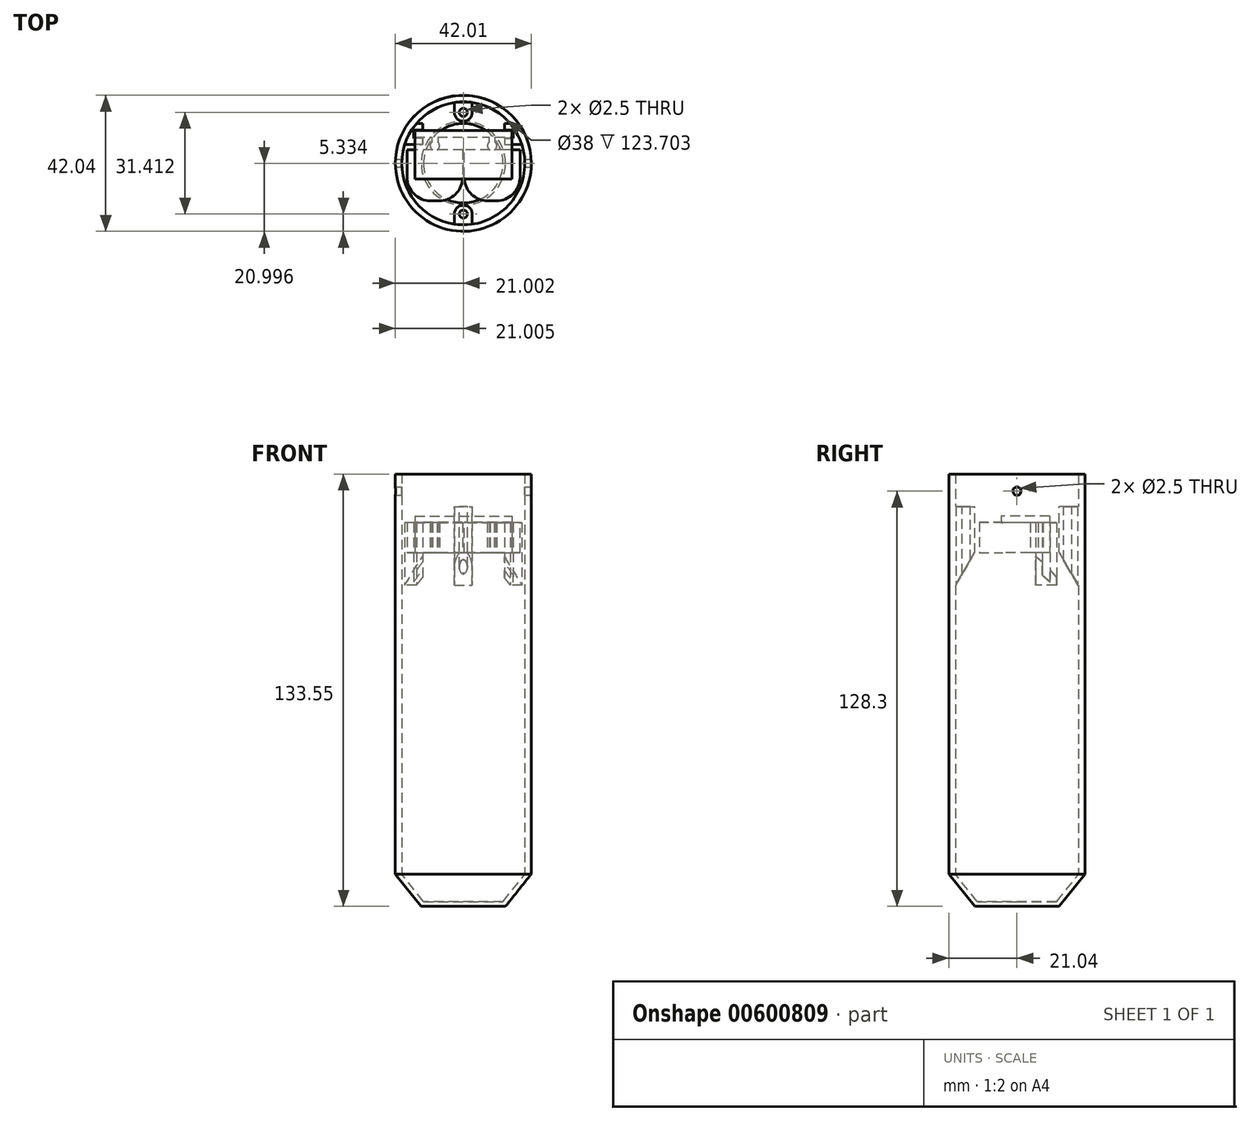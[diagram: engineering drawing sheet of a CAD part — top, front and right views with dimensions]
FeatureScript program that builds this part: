
annotation { "Feature Type Name" : "Feature", "Feature Type Description" : "" }
export const myFeature = defineFeature(function(context is Context, id is Id, definition is map)
    precondition{}
    {
        {
            var Q0;
            Q0=qCreatedBy(makeId("Front.planeOp"),FACE);
            var sketch = newSketch(context, id + "F0", { "sketchPlane" : qUnion([Q0])});
            skLineSegment(sketch, "E0.bottom", {"start": v(-22.87, 37.15) * mm, "end": v(-5.67, 37.15) * mm});
            skLineSegment(sketch, "E0.top", {"start": v(-22.87, -71.55) * mm, "end": v(-5.67, -71.55) * mm});
            skLineSegment(sketch, "E0.left", {"start": v(-22.87, 37.15) * mm, "end": v(-22.87, -71.55) * mm});
            skLineSegment(sketch, "E0.right", {"start": v(-5.67, 37.15) * mm, "end": v(-5.67, -71.55) * mm});
            skLineSegment(sketch, "E1.bottom", {"start": v(-5.17, -71.55) * mm, "end": v(12.03, -71.55) * mm});
            skLineSegment(sketch, "E1.top", {"start": v(-5.17, 37.15) * mm, "end": v(12.03, 37.15) * mm});
            skLineSegment(sketch, "E1.left", {"start": v(-5.17, -71.55) * mm, "end": v(-5.17, 37.15) * mm});
            skLineSegment(sketch, "E1.right", {"start": v(12.03, -71.55) * mm, "end": v(12.03, 37.15) * mm});
            skSolve(sketch);
        }
        {
            var Q0;
            Q0=makeQuery(id+"F0.imprint","IMPRINT",FACE,{"disambiguationData":[TD([[makeQuery(id+"F0.imprint","IMPRINT",EDGE,{"derivedFrom":sQuery(id+"F0.wireOp",EDGE,"E0.bottom")}),-1.0]])]});
            var Q1;
            Q1=makeQuery(id+"F0.imprint","IMPRINT",FACE,{"disambiguationData":[TD([[makeQuery(id+"F0.imprint","IMPRINT",EDGE,{"derivedFrom":sQuery(id+"F0.wireOp",EDGE,"E1.bottom")}),1.0]])]});
            extrude(context, id + "F1", {"entities" : qUnion([Q0, Q1]), "depth" : 15.75 * mm, "offsetDistance" : 25 * mm});
        }
        {
            var Q0;
            Q0=makeQuery(id+"F1.opExtrude","CAP_EDGE",EDGE,{"disambiguationData":[OSD([sQuery(id+"F0.wireOp",EDGE,"E0.left")])],"isStart":false});
            var Q1;
            Q1=makeQuery(id+"F1.opExtrude","CAP_EDGE",EDGE,{"disambiguationData":[OSD([sQuery(id+"F0.wireOp",EDGE,"E0.right")])],"isStart":false});
            var Q2;
            Q2=makeQuery(id+"F1.opExtrude","CAP_EDGE",EDGE,{"disambiguationData":[OSD([sQuery(id+"F0.wireOp",EDGE,"E1.left")])],"isStart":false});
            var Q3;
            Q3=makeQuery(id+"F1.opExtrude","CAP_EDGE",EDGE,{"disambiguationData":[OSD([sQuery(id+"F0.wireOp",EDGE,"E1.right")])],"isStart":false});
            fillet(context, id + "F2", {"entities" : qUnion([Q0, Q1, Q2, Q3]), "radius" : 7.3 * mm, "tangentPropagation" : true, "allowEdgeOverflow" : false});
        }
        {
            var Q0;
            Q0=makeQuery(id+"F1.opExtrude","CAP_FACE",FACE,{"disambiguationData":[OSD([sQuery(id+"F0.wireOp",EDGE,"E0.bottom"),sQuery(id+"F0.wireOp",EDGE,"E0.top"),sQuery(id+"F0.wireOp",EDGE,"E0.left"),sQuery(id+"F0.wireOp",EDGE,"E0.right")])],"isStart":true});
            var sketch = newSketch(context, id + "F3", { "sketchPlane" : qUnion([Q0])});
            skLineSegment(sketch, "E2.bottom", {"start": v(11.37, 24.15) * mm, "end": v(17.17, 24.15) * mm});
            skLineSegment(sketch, "E2.top", {"start": v(11.37, 20.15) * mm, "end": v(17.17, 20.15) * mm});
            skLineSegment(sketch, "E2.left", {"start": v(11.37, 24.15) * mm, "end": v(11.37, 20.15) * mm});
            skLineSegment(sketch, "E2.right", {"start": v(17.17, 24.15) * mm, "end": v(17.17, 20.15) * mm});
            skLineSegment(sketch, "E3.bottom", {"start": v(11.37, -15.1) * mm, "end": v(17.17, -15.1) * mm});
            skLineSegment(sketch, "E3.top", {"start": v(11.37, -19.1) * mm, "end": v(17.17, -19.1) * mm});
            skLineSegment(sketch, "E3.left", {"start": v(11.37, -15.1) * mm, "end": v(11.37, -19.1) * mm});
            skLineSegment(sketch, "E3.right", {"start": v(17.17, -15.1) * mm, "end": v(17.17, -19.1) * mm});
            skLineSegment(sketch, "E4.bottom", {"start": v(11.37, -54.35) * mm, "end": v(17.17, -54.35) * mm});
            skLineSegment(sketch, "E4.top", {"start": v(11.37, -58.35) * mm, "end": v(17.17, -58.35) * mm});
            skLineSegment(sketch, "E4.left", {"start": v(11.37, -54.35) * mm, "end": v(11.37, -58.35) * mm});
            skLineSegment(sketch, "E4.right", {"start": v(17.17, -54.35) * mm, "end": v(17.17, -58.35) * mm});
            skLineSegment(sketch, "E5.bottom", {"start": v(-6.33, 24.15) * mm, "end": v(-0.53, 24.15) * mm});
            skLineSegment(sketch, "E5.top", {"start": v(-6.33, 20.15) * mm, "end": v(-0.53, 20.15) * mm});
            skLineSegment(sketch, "E5.left", {"start": v(-6.33, 24.15) * mm, "end": v(-6.33, 20.15) * mm});
            skLineSegment(sketch, "E5.right", {"start": v(-0.53, 24.15) * mm, "end": v(-0.53, 20.15) * mm});
            skPoint(sketch, "E6.oppositeSnap0", {"position": v(-0.53, 22.15) * mm});
            skLineSegment(sketch, "E6.bottom", {"start": v(-6.33, -15.1) * mm, "end": v(-0.53, -15.1) * mm});
            skLineSegment(sketch, "E6.top", {"start": v(-6.33, -19.1) * mm, "end": v(-0.53, -19.1) * mm});
            skLineSegment(sketch, "E6.left", {"start": v(-6.33, -15.1) * mm, "end": v(-6.33, -19.1) * mm});
            skLineSegment(sketch, "E6.right", {"start": v(-0.53, -15.1) * mm, "end": v(-0.53, -19.1) * mm});
            skLineSegment(sketch, "E7.bottom", {"start": v(-6.33, -54.35) * mm, "end": v(-0.53, -54.35) * mm});
            skLineSegment(sketch, "E7.top", {"start": v(-6.33, -58.35) * mm, "end": v(-0.53, -58.35) * mm});
            skLineSegment(sketch, "E7.left", {"start": v(-6.33, -54.35) * mm, "end": v(-6.33, -58.35) * mm});
            skLineSegment(sketch, "E7.right", {"start": v(-0.53, -54.35) * mm, "end": v(-0.53, -58.35) * mm});
            skSolve(sketch);
        }
        {
            var Q0;
            Q0=makeQuery(id+"F3.imprint","IMPRINT",FACE,{"disambiguationData":[TD([[makeQuery(id+"F3.imprint","IMPRINT",EDGE,{"derivedFrom":sQuery(id+"F3.wireOp",EDGE,"E5.bottom")}),-1.0]])]});
            var Q1;
            Q1=makeQuery(id+"F3.imprint","IMPRINT",FACE,{"disambiguationData":[TD([[makeQuery(id+"F3.imprint","IMPRINT",EDGE,{"derivedFrom":sQuery(id+"F3.wireOp",EDGE,"E2.bottom")}),-1.0]])]});
            var Q2;
            Q2=makeQuery(id+"F3.imprint","IMPRINT",FACE,{"disambiguationData":[TD([[makeQuery(id+"F3.imprint","IMPRINT",EDGE,{"derivedFrom":sQuery(id+"F3.wireOp",EDGE,"E6.bottom")}),-1.0]])]});
            var Q3;
            Q3=makeQuery(id+"F3.imprint","IMPRINT",FACE,{"disambiguationData":[TD([[makeQuery(id+"F3.imprint","IMPRINT",EDGE,{"derivedFrom":sQuery(id+"F3.wireOp",EDGE,"E3.bottom")}),-1.0]])]});
            var Q4;
            Q4=makeQuery(id+"F3.imprint","IMPRINT",FACE,{"disambiguationData":[TD([[makeQuery(id+"F3.imprint","IMPRINT",EDGE,{"derivedFrom":sQuery(id+"F3.wireOp",EDGE,"E7.bottom")}),-1.0]])]});
            var Q5;
            Q5=makeQuery(id+"F3.imprint","IMPRINT",FACE,{"disambiguationData":[TD([[makeQuery(id+"F3.imprint","IMPRINT",EDGE,{"derivedFrom":sQuery(id+"F3.wireOp",EDGE,"E4.bottom")}),-1.0]])]});
            extrude(context, id + "F4", {"entities" : qUnion([Q0, Q1, Q2, Q3, Q4, Q5]), "depth" : 3 * mm, "offsetDistance" : 25 * mm});
        }
        {
            var Q0;
            Q0=makeQuery(id+"F4.opExtrude","SWEPT_FACE",FACE,{"disambiguationData":[OSD([sQuery(id+"F3.wireOp",EDGE,"E2.bottom")])]});
            var sketch = newSketch(context, id + "F5", { "sketchPlane" : qUnion([Q0])});
            skCircle(sketch, "E8", {"center": v(-14.27, 1.3) * mm, "radius": 2 * mm});
            skPoint(sketch, "E8.centerSnap0", {"position": v(-14.27, 0) * mm});
            skCircle(sketch, "E9", {"center": v(3.43, 1.3) * mm, "radius": 2 * mm});
            skLineSegment(sketch, "E10", {"start": v(3.43, -0.32) * mm, "end": v(3.43, 2.34) * mm, "construction": true});
            skLineSegment(sketch, "E11", {"start": v(-14.27, 1.3) * mm, "end": v(3.43, 1.3) * mm, "construction": true});
            skSolve(sketch);
        }
        {
            var Q0;
            {var subQ0=sQuery(id+"F5.wireOp",EDGE,"E8");var subQ1=sQuery(id+"F3.wireOp",EDGE,"E2.bottom");var subQ2=makeQuery(id+"F4.opExtrude","CAP_EDGE",EDGE,{"disambiguationData":[OSD([subQ1])],"isStart":false});var subQ3=makeQuery(id+"F5.imprint","INTERSECT",VERTEX,{"disambiguationData":[OD(0.0)],"derivedFrom":[subQ2,subQ0]});Q0=makeQuery(id+"F5.imprint","IMPRINT",FACE,{"disambiguationData":[TD([[makeQuery(id+"F5.imprint","IMPRINT",EDGE,{"disambiguationData":[TD([[subQ3,-1.0]])],"derivedFrom":subQ0}),1.0]])]});}
            extrude(context, id + "F6", {"entities" : qUnion([Q0]), "operationType" : NewBodyOperationType.REMOVE, "oppositeDirection" : true, "depth" : 111.1 * mm, "offsetDistance" : 25 * mm});
        }
        {
            var Q0;
            Q0=makeQuery(id+"F5.imprint","IMPRINT",FACE,{"disambiguationData":[TD([[makeQuery(id+"F5.imprint","IMPRINT",EDGE,{"derivedFrom":sQuery(id+"F5.wireOp",EDGE,"E9")}),1.0]])]});
            extrude(context, id + "F7", {"entities" : qUnion([Q0]), "operationType" : NewBodyOperationType.REMOVE, "oppositeDirection" : true, "depth" : 101.7 * mm, "offsetDistance" : 25 * mm});
        }
        {
            var Q0;
            Q0=makeQuery(id+"F4.opExtrude","CAP_EDGE",EDGE,{"disambiguationData":[OSD([sQuery(id+"F3.wireOp",EDGE,"E2.left")])],"isStart":false});
            var Q1;
            Q1=makeQuery(id+"F4.opExtrude","CAP_EDGE",EDGE,{"disambiguationData":[OSD([sQuery(id+"F3.wireOp",EDGE,"E2.right")])],"isStart":false});
            var Q2;
            Q2=makeQuery(id+"F4.opExtrude","CAP_EDGE",EDGE,{"disambiguationData":[OSD([sQuery(id+"F3.wireOp",EDGE,"E3.left")])],"isStart":false});
            var Q3;
            Q3=makeQuery(id+"F4.opExtrude","CAP_EDGE",EDGE,{"disambiguationData":[OSD([sQuery(id+"F3.wireOp",EDGE,"E3.right")])],"isStart":false});
            var Q4;
            Q4=makeQuery(id+"F4.opExtrude","CAP_EDGE",EDGE,{"disambiguationData":[OSD([sQuery(id+"F3.wireOp",EDGE,"E4.left")])],"isStart":false});
            var Q5;
            Q5=makeQuery(id+"F4.opExtrude","CAP_EDGE",EDGE,{"disambiguationData":[OSD([sQuery(id+"F3.wireOp",EDGE,"E4.right")])],"isStart":false});
            var Q6;
            Q6=makeQuery(id+"F4.opExtrude","CAP_EDGE",EDGE,{"disambiguationData":[OSD([sQuery(id+"F3.wireOp",EDGE,"E7.left")])],"isStart":false});
            var Q7;
            Q7=makeQuery(id+"F4.opExtrude","CAP_EDGE",EDGE,{"disambiguationData":[OSD([sQuery(id+"F3.wireOp",EDGE,"E7.right")])],"isStart":false});
            var Q8;
            Q8=makeQuery(id+"F4.opExtrude","CAP_EDGE",EDGE,{"disambiguationData":[OSD([sQuery(id+"F3.wireOp",EDGE,"E6.left")])],"isStart":false});
            var Q9;
            Q9=makeQuery(id+"F4.opExtrude","CAP_EDGE",EDGE,{"disambiguationData":[OSD([sQuery(id+"F3.wireOp",EDGE,"E6.right")])],"isStart":false});
            var Q10;
            Q10=makeQuery(id+"F4.opExtrude","CAP_EDGE",EDGE,{"disambiguationData":[OSD([sQuery(id+"F3.wireOp",EDGE,"E5.left")])],"isStart":false});
            var Q11;
            Q11=makeQuery(id+"F4.opExtrude","CAP_EDGE",EDGE,{"disambiguationData":[OSD([sQuery(id+"F3.wireOp",EDGE,"E5.right")])],"isStart":false});
            fillet(context, id + "F8", {"entities" : qUnion([Q0, Q1, Q2, Q3, Q4, Q5, Q6, Q7, Q8, Q9, Q10, Q11]), "radius" : 1.5 * mm, "tangentPropagation" : true, "allowEdgeOverflow" : false});
        }
        {
            var Q0;
            Q0=qCreatedBy(makeId("Top.planeOp"),FACE);
            var sketch = newSketch(context, id + "F9", { "sketchPlane" : qUnion([Q0])});
            skLineSegment(sketch, "E12.left", {"start": v(-15.16, 4) * mm, "end": v(-15.16, 2.44) * mm});
            skLineSegment(sketch, "E12.right", {"start": v(-13.36, 4) * mm, "end": v(-13.36, 2.44) * mm});
            skLineSegment(sketch, "E13.left", {"start": v(2.53, 2.44) * mm, "end": v(2.53, 4) * mm});
            skLineSegment(sketch, "E13.right", {"start": v(4.33, 2.44) * mm, "end": v(4.33, 4) * mm});
            skLineSegment(sketch, "E14.bottom", {"start": v(-20.42, 6) * mm, "end": v(-13.36, 6) * mm});
            skLineSegment(sketch, "E14.top", {"start": v(-20.42, 4) * mm, "end": v(-15.16, 4) * mm});
            skLineSegment(sketch, "E14.left", {"start": v(-20.42, 6) * mm, "end": v(-20.42, 4) * mm});
            skLineSegment(sketch, "E14.right", {"start": v(9.58, 6) * mm, "end": v(9.58, 4) * mm});
            skLineSegment(sketch, "E15.trimOffspring", {"start": v(-13.36, 6) * mm, "end": v(9.58, 6) * mm});
            skPoint(sketch, "E16.orphan", {"position": v(-15.16, 6) * mm});
            skLineSegment(sketch, "E17.trimOffspring", {"start": v(-13.36, 4) * mm, "end": v(2.53, 4) * mm});
            skPoint(sketch, "E18.orphan", {"position": v(2.53, 2.24) * mm});
            skLineSegment(sketch, "E19.trimOffspring", {"start": v(4.33, 4) * mm, "end": v(9.58, 4) * mm});
            skPoint(sketch, "E20.center.orphan", {"position": v(3.43, 1.3) * mm});
            skArc(sketch, "E21", {"start": v(2.53, 2.44) * mm, "mid": v(3.43, -0.15) * mm, "end": v(4.33, 2.44) * mm});
            skPoint(sketch, "E22.center.orphan", {"position": v(-14.26, 1.3) * mm});
            skArc(sketch, "E23", {"start": v(-15.16, 2.44) * mm, "mid": v(-14.26, -0.15) * mm, "end": v(-13.36, 2.44) * mm});
            skSolve(sketch);
        }
        {
            var Q0;
            Q0=makeQuery(id+"F9.imprint","IMPRINT",FACE,{"disambiguationData":[TD([[makeQuery(id+"F9.imprint","IMPRINT",EDGE,{"derivedFrom":sQuery(id+"F9.wireOp",EDGE,"E12.left")}),1.0]])]});
            extrude(context, id + "F10", {"entities" : qUnion([Q0]), "depth" : 37 * mm, "offsetDistance" : 25 * mm, "hasSecondDirection" : true, "secondDirectionOppositeDirection" : true, "secondDirectionDepth" : 72 * mm});
        }
        {
            var Q0;
            Q0=makeQuery(id+"F10.opExtrude","CAP_FACE",FACE,{"disambiguationData":[OSD([sQuery(id+"F9.wireOp",EDGE,"E12.left"),sQuery(id+"F9.wireOp",EDGE,"E12.right"),sQuery(id+"F9.wireOp",EDGE,"E13.left"),sQuery(id+"F9.wireOp",EDGE,"E13.right"),sQuery(id+"F9.wireOp",EDGE,"E14.bottom"),sQuery(id+"F9.wireOp",EDGE,"E14.top"),sQuery(id+"F9.wireOp",EDGE,"E14.left"),sQuery(id+"F9.wireOp",EDGE,"E14.right"),sQuery(id+"F9.wireOp",EDGE,"E15.trimOffspring"),sQuery(id+"F9.wireOp",EDGE,"E17.trimOffspring"),sQuery(id+"F9.wireOp",EDGE,"E19.trimOffspring"),sQuery(id+"F9.wireOp",EDGE,"E21"),sQuery(id+"F9.wireOp",EDGE,"E23")])],"isStart":false});
            var sketch = newSketch(context, id + "F11", { "sketchPlane" : qUnion([Q0])});
            skLineSegment(sketch, "E24.bottom", {"start": v(-20.42, 6) * mm, "end": v(9.58, 6) * mm});
            skLineSegment(sketch, "E24.top", {"start": v(-20.42, -9) * mm, "end": v(9.58, -9) * mm});
            skLineSegment(sketch, "E24.left", {"start": v(-20.42, -9) * mm, "end": v(-20.42, 6) * mm});
            skLineSegment(sketch, "E24.right", {"start": v(9.58, -9) * mm, "end": v(9.58, 6) * mm});
            skSolve(sketch);
        }
        {
            var Q0;
            Q0 = qSketchRegion(id + "F11", true);
            extrude(context, id + "F12", {"entities" : qUnion([Q0]), "operationType" : NewBodyOperationType.ADD, "depth" : 2 * mm, "offsetDistance" : 25 * mm});
        }
        {
            var Q0;
            Q0=makeQuery(id+"F1.opExtrude","SWEPT_FACE",FACE,{"disambiguationData":[OSD([sQuery(id+"F0.wireOp",EDGE,"E0.top")])]});
            cPlane(context, id + "F13", {"entities" : qUnion([Q0]), "cplaneType" : CPlaneType.OFFSET, "offset" : 0 * mm, "width" : 150 * mm, "height" : 150 * mm});
        }
        {
            var Q0;
            Q0=qCreatedBy(id+"F13.planeOp",FACE);
            var sketch = newSketch(context, id + "F14", { "sketchPlane" : qUnion([Q0])});
            skLineSegment(sketch, "E25", {"start": v(-18.07, -3.65) * mm, "end": v(-20.77, -3.65) * mm});
            skLineSegment(sketch, "E26", {"start": v(-20.77, -6.15) * mm, "end": v(-18.07, -6.15) * mm});
            skLineSegment(sketch, "E27", {"start": v(-18.07, -6.15) * mm, "end": v(-18.07, -8.15) * mm});
            skLineSegment(sketch, "E28", {"start": v(-18.07, -8.15) * mm, "end": v(-19.95, -8.15) * mm});
            skLineSegment(sketch, "E29", {"start": v(-18.07, -3.65) * mm, "end": v(-18.07, -1.65) * mm});
            skLineSegment(sketch, "E30", {"start": v(-18.07, -1.65) * mm, "end": v(-23.56, -1.65) * mm});
            skLineSegment(sketch, "E31", {"start": v(7.23, -3.65) * mm, "end": v(9.93, -3.65) * mm});
            skLineSegment(sketch, "E32", {"start": v(9.93, -6.15) * mm, "end": v(7.23, -6.15) * mm});
            skLineSegment(sketch, "E33", {"start": v(7.23, -6.15) * mm, "end": v(7.23, -8.15) * mm});
            skLineSegment(sketch, "E34", {"start": v(7.23, -8.15) * mm, "end": v(9.02, -8.15) * mm});
            skLineSegment(sketch, "E35", {"start": v(7.23, -3.65) * mm, "end": v(7.23, -1.65) * mm});
            skLineSegment(sketch, "E36", {"start": v(7.23, -1.65) * mm, "end": v(12.63, -1.65) * mm});
            skArc(sketch, "E37", {"start": v(-19.95, -8.15) * mm, "mid": v(-5.47, -14.86) * mm, "end": v(9.02, -8.15) * mm});
            skPoint(sketch, "E38.orphan", {"position": v(10.48, -1.65) * mm});
            skPoint(sketch, "E39.orphan", {"position": v(-24.4, -1.65) * mm});
            skPoint(sketch, "E40.orphan", {"position": v(-24.4, -8.15) * mm});
            skPoint(sketch, "E41.orphan", {"position": v(10.48, -8.15) * mm});
            skCircle(sketch, "E42", {"center": v(-5.47, 4.14) * mm, "radius": 21 * mm});
            skArc(sketch, "E43.trimOffspring", {"start": v(12.63, -1.65) * mm, "mid": v(-5.47, 23.14) * mm, "end": v(-23.56, -1.65) * mm});
            skLineSegment(sketch, "E44", {"start": v(9.93, -6.15) * mm, "end": v(9.93, -3.65) * mm});
            skLineSegment(sketch, "E45", {"start": v(-20.77, -6.15) * mm, "end": v(-20.77, -3.65) * mm});
            skSolve(sketch);
        }
        {
            var Q0;
            Q0=makeQuery(id+"F14.imprint","IMPRINT",FACE,{"disambiguationData":[TD([[makeQuery(id+"F14.imprint","IMPRINT",EDGE,{"derivedFrom":sQuery(id+"F14.wireOp",EDGE,"E25")}),-1.0]])]});
            var Q1;
            Q1=makeQuery(id+"F12.opExtrude","CAP_FACE",FACE,{"disambiguationData":[OSD([sQuery(id+"F11.wireOp",EDGE,"E24.bottom"),sQuery(id+"F11.wireOp",EDGE,"E24.top"),sQuery(id+"F11.wireOp",EDGE,"E24.left"),sQuery(id+"F11.wireOp",EDGE,"E24.right")])],"isStart":true});
            extrude(context, id + "F15", {"entities" : qUnion([Q0]), "endBound" : BoundingType.UP_TO_SURFACE, "oppositeDirection" : true, "depth" : 107.8 * mm, "endBoundEntityFace" : qUnion([Q1]), "offsetDistance" : 25 * mm});
        }
        {
            var Q0;
            Q0=makeQuery(id+"F15.opExtrude","CAP_FACE",FACE,{"disambiguationData":[OSD([sQuery(id+"F14.wireOp",EDGE,"E25"),sQuery(id+"F14.wireOp",EDGE,"E26"),sQuery(id+"F14.wireOp",EDGE,"E27"),sQuery(id+"F14.wireOp",EDGE,"E28"),sQuery(id+"F14.wireOp",EDGE,"E29"),sQuery(id+"F14.wireOp",EDGE,"E30"),sQuery(id+"F14.wireOp",EDGE,"E31"),sQuery(id+"F14.wireOp",EDGE,"E32"),sQuery(id+"F14.wireOp",EDGE,"E33"),sQuery(id+"F14.wireOp",EDGE,"E34"),sQuery(id+"F14.wireOp",EDGE,"E35"),sQuery(id+"F14.wireOp",EDGE,"E36"),sQuery(id+"F14.wireOp",EDGE,"E37"),sQuery(id+"F14.wireOp",EDGE,"E42"),sQuery(id+"F14.wireOp",EDGE,"E43.trimOffspring"),sQuery(id+"F14.wireOp",EDGE,"E44"),sQuery(id+"F14.wireOp",EDGE,"E45")])],"isStart":false});
            var sketch = newSketch(context, id + "F16", { "sketchPlane" : qUnion([Q0])});
            skCircle(sketch, "E46", {"center": v(-5.47, -4.14) * mm, "radius": 21 * mm});
            skCircle(sketch, "E47", {"center": v(-5.47, -4.14) * mm, "radius": 19 * mm});
            skSolve(sketch);
        }
        {
            var Q0;
            Q0=makeQuery(id+"F16.imprint","IMPRINT",FACE,{"disambiguationData":[TD([[makeQuery(id+"F16.imprint","IMPRINT",EDGE,{"derivedFrom":sQuery(id+"F16.wireOp",EDGE,"E46")}),-1.0]])]});
            extrude(context, id + "F17", {"entities" : qUnion([Q0]), "operationType" : NewBodyOperationType.ADD, "depth" : 15 * mm, "offsetDistance" : 25 * mm});
        }
        {
            var Q0;
            Q0=qCreatedBy(makeId("Right.planeOp"),FACE);
            cPlane(context, id + "F18", {"entities" : qUnion([Q0]), "cplaneType" : CPlaneType.OFFSET, "offset" : 5.46 * mm, "oppositeDirection" : true, "width" : 150 * mm, "height" : 150 * mm});
        }
        {
            var Q0;
            Q0=qCreatedBy(makeId("Front.planeOp"),FACE);
            cPlane(context, id + "F19", {"entities" : qUnion([Q0]), "cplaneType" : CPlaneType.OFFSET, "offset" : 4.1 * mm, "width" : 150 * mm, "height" : 150 * mm});
        }
        {
            var Q0;
            Q0=qCreatedBy(id+"F19.planeOp",FACE);
            var sketch = newSketch(context, id + "F20", { "sketchPlane" : qUnion([Q0])});
            skLineSegment(sketch, "E48", {"start": v(-5.47, 75.54) * mm, "end": v(-5.46, -79.75) * mm, "construction": true});
            skSolve(sketch);
        }
        {
            var Q0;
            Q0=qCreatedBy(id+"F19.planeOp",FACE);
            var sketch = newSketch(context, id + "F21", { "sketchPlane" : qUnion([Q0])});
            skLineSegment(sketch, "E49", {"start": v(-26.46, -71.55) * mm, "end": v(-18.46, -81.55) * mm});
            skLineSegment(sketch, "E50", {"start": v(-18.46, -81.55) * mm, "end": v(-5.46, -81.55) * mm});
            skLineSegment(sketch, "E51", {"start": v(-5.46, -81.55) * mm, "end": v(-5.46, -80.05) * mm});
            skLineSegment(sketch, "E52", {"start": v(-5.46, -80.05) * mm, "end": v(-17.74, -80.05) * mm});
            skLineSegment(sketch, "E53", {"start": v(-17.74, -80.05) * mm, "end": v(-24.54, -71.55) * mm});
            skLineSegment(sketch, "E54", {"start": v(-26.46, -71.55) * mm, "end": v(-24.54, -71.55) * mm});
            skSolve(sketch);
        }
        {
            var Q0;
            Q0=makeQuery(id+"F21.imprint","IMPRINT",FACE,{"disambiguationData":[TD([[makeQuery(id+"F21.imprint","IMPRINT",EDGE,{"derivedFrom":sQuery(id+"F21.wireOp",EDGE,"E49")}),1.0]])]});
            var Q1;
            Q1=sQuery(id+"F20.wireOp",EDGE,"E48");
            revolve(context, id + "F22", {"operationType" : NewBodyOperationType.ADD, "entities" : qUnion([Q0]), "axis" : qUnion([Q1]), "revolveType" : RevolveType.FULL});
        }
        {
            var Q0;
            Q0=makeQuery(id+"F17.opExtrude","CAP_FACE",FACE,{"disambiguationData":[OSD([sQuery(id+"F16.wireOp",EDGE,"E46"),sQuery(id+"F16.wireOp",EDGE,"E47")])],"isStart":false});
            cPlane(context, id + "F23", {"entities" : qUnion([Q0]), "cplaneType" : CPlaneType.OFFSET, "offset" : 10 * mm, "oppositeDirection" : true, "width" : 150 * mm, "height" : 150 * mm});
        }
        {
            var Q0;
            Q0=qCreatedBy(id+"F23.planeOp",FACE);
            var sketch = newSketch(context, id + "F24", { "sketchPlane" : qUnion([Q0])});
            skArc(sketch, "E55", {"start": v(-8.21, 11.6) * mm, "mid": v(-5.46, 8.86) * mm, "end": v(-2.72, 11.6) * mm});
            skCircle(sketch, "E56", {"center": v(-5.46, 11.6) * mm, "radius": 1.25 * mm});
            skLineSegment(sketch, "E57", {"start": v(-8.21, 11.6) * mm, "end": v(-8.21, 15.32) * mm});
            skLineSegment(sketch, "E58", {"start": v(-8.21, 15.32) * mm, "end": v(-2.72, 15.32) * mm});
            skLineSegment(sketch, "E59", {"start": v(-2.72, 15.32) * mm, "end": v(-2.71, 11.6) * mm});
            skLineSegment(sketch, "E60.MirrorCS", {"start": v(-8.21, -19.8) * mm, "end": v(-8.21, -23.52) * mm});
            skLineSegment(sketch, "E61.MirrorCS", {"start": v(-2.72, -23.52) * mm, "end": v(-2.71, -19.8) * mm});
            skLineSegment(sketch, "E62.MirrorCS", {"start": v(-8.21, -23.52) * mm, "end": v(-2.72, -23.52) * mm});
            skArc(sketch, "E63.MirrorCS", {"start": v(-8.21, -19.8) * mm, "mid": v(-5.46, -17.06) * mm, "end": v(-2.72, -19.8) * mm});
            skCircle(sketch, "E64.MirrorC", {"center": v(-5.46, -19.8) * mm, "radius": 1.25 * mm});
            skSolve(sketch);
        }
        {
            var Q0;
            Q0=makeQuery(id+"F24.imprint","IMPRINT",FACE,{"disambiguationData":[TD([[makeQuery(id+"F24.imprint","IMPRINT",EDGE,{"derivedFrom":sQuery(id+"F24.wireOp",EDGE,"E55")}),1.0]])]});
            var Q1;
            Q1=makeQuery(id+"F24.imprint","IMPRINT",FACE,{"disambiguationData":[TD([[makeQuery(id+"F24.imprint","IMPRINT",EDGE,{"derivedFrom":sQuery(id+"F24.wireOp",EDGE,"E60.MirrorCS")}),1.0]])]});
            extrude(context, id + "F25", {"entities" : qUnion([Q0, Q1]), "operationType" : NewBodyOperationType.ADD, "endBound" : BoundingType.UP_TO_NEXT, "oppositeDirection" : true, "depth" : 41.9 * mm, "offsetDistance" : 25 * mm});
        }
        {
            var Q0;
            Q0=qCreatedBy(makeId("Right.planeOp"),FACE);
            var sketch = newSketch(context, id + "F26", { "sketchPlane" : qUnion([Q0])});
            skCircle(sketch, "E65", {"center": v(-4.1, 46.75) * mm, "radius": 1.25 * mm});
            skSolve(sketch);
        }
        {
            var Q0;
            Q0 = qSketchRegion(id + "F26", true);
            extrude(context, id + "F27", {"entities" : qUnion([Q0]), "operationType" : NewBodyOperationType.REMOVE, "oppositeDirection" : true, "depth" : 33 * mm, "offsetDistance" : 25 * mm, "hasSecondDirection" : true, "secondDirectionOppositeDirection" : false, "secondDirectionDepth" : 31 * mm});
        }
        {
            var Q0;
            Q0=qCreatedBy(makeId("Top.planeOp"),FACE);
            cPlane(context, id + "F28", {"entities" : qUnion([Q0]), "cplaneType" : CPlaneType.OFFSET, "offset" : 25 * mm, "width" : 150 * mm, "height" : 150 * mm});
        }
        {
            var Q0;
            Q0=qCreatedBy(id+"F28.planeOp",FACE);
            var sketch = newSketch(context, id + "F29", { "sketchPlane" : qUnion([Q0])});
            skCircle(sketch, "E66.0", {"center": v(-5.47, -4.14) * mm, "radius": 19 * mm});
            skSolve(sketch);
        }
        {
            var Q0;
            Q0=makeQuery(id+"F29.imprint","IMPRINT",FACE,{"disambiguationData":[TD([[makeQuery(id+"F29.imprint","IMPRINT",EDGE,{"derivedFrom":sQuery(id+"F29.wireOp",EDGE,"E66.0")}),1.0]])]});
            var Q1;
            Q1=makeQuery(id+"F25.boolean.opBoolean","SPLIT",FACE,{"disambiguationData":[TD([makeQuery(id+"F22.opRevolve","SWEPT_FACE",FACE,{"disambiguationData":[OSD([sQuery(id+"F21.wireOp",EDGE,"E52")])]})])],"derivedFrom":makeQuery(id+"F22.opRevolve","SWEPT_FACE",FACE,{"disambiguationData":[OSD([sQuery(id+"F21.wireOp",EDGE,"E53")])]})});
            extrude(context, id + "F30", {"entities" : qUnion([Q0]), "operationType" : NewBodyOperationType.REMOVE, "endBound" : BoundingType.UP_TO_SURFACE, "oppositeDirection" : true, "depth" : 44.9 * mm, "endBoundEntityFace" : qUnion([Q1]), "offsetDistance" : 25 * mm, "hasSecondDirection" : true, "secondDirectionOppositeDirection" : false, "secondDirectionDepth" : 2.7 * mm});
        }
        {
            var Q0;
            {var subQ0=sQuery(id+"F29.wireOp",EDGE,"E66.0");Q0=makeQuery(id+"F30.boolean.opBoolean","COPY",EDGE,{"disambiguationData":[TD([makeQuery(id+"F15.opExtrude","SWEPT_FACE",FACE,{"disambiguationData":[OSD([sQuery(id+"F14.wireOp",EDGE,"E34")])]})])],"derivedFrom":makeQuery(id+"F30.opExtrude","CAP_EDGE",EDGE,{"disambiguationData":[OSD([subQ0])],"isStart":true})});}
            var Q1;
            {var subQ0=sQuery(id+"F29.wireOp",EDGE,"E66.0");Q1=makeQuery(id+"F30.boolean.opBoolean","COPY",EDGE,{"disambiguationData":[TD([makeQuery(id+"F15.opExtrude","SWEPT_FACE",FACE,{"disambiguationData":[OSD([sQuery(id+"F14.wireOp",EDGE,"E28")])]})])],"derivedFrom":makeQuery(id+"F30.opExtrude","CAP_EDGE",EDGE,{"disambiguationData":[OSD([subQ0])],"isStart":true})});}
            chamfer(context, id + "F31", {"entities" : qUnion([Q0, Q1]), "chamferType" : ChamferType.OFFSET_ANGLE, "width" : 10 * mm, "oppositeDirection" : false, "angle" : 30 * degree, "tangentPropagation" : true});
        }
        {
            var Q0;
            Q0=makeQuery(id+"F22.opRevolve","SWEPT_FACE",FACE,{"disambiguationData":[OSD([sQuery(id+"F21.wireOp",EDGE,"E50")])]});
            var sketch = newSketch(context, id + "F32", { "sketchPlane" : qUnion([Q0])});
            skCircle(sketch, "E67.0", {"center": v(-5.47, 4.1) * mm, "radius": 13 * mm});
            skSolve(sketch);
        }
        {
            var Q0;
            Q0 = qSketchRegion(id + "F32", true);
            extrude(context, id + "F33", {"entities" : qUnion([Q0]), "operationType" : NewBodyOperationType.ADD, "oppositeDirection" : true, "depth" : 1.5 * mm, "offsetDistance" : 25 * mm});
        }
        {
            var Q0;
            {var subQ0=sQuery(id+"F29.wireOp",EDGE,"E66.0");Q0=makeQuery(id+"F30.boolean.opBoolean","COPY",EDGE,{"disambiguationData":[TD([makeQuery(id+"F25.opExtrude","SWEPT_FACE",FACE,{"disambiguationData":[OSD([sQuery(id+"F24.wireOp",EDGE,"E57")])]})])],"derivedFrom":makeQuery(id+"F30.opExtrude","CAP_EDGE",EDGE,{"disambiguationData":[OSD([subQ0])],"isStart":true})});}
            var Q1;
            {var subQ0=sQuery(id+"F29.wireOp",EDGE,"E66.0");Q1=makeQuery(id+"F30.boolean.opBoolean","COPY",EDGE,{"disambiguationData":[TD([makeQuery(id+"F25.opExtrude","SWEPT_FACE",FACE,{"disambiguationData":[OSD([sQuery(id+"F24.wireOp",EDGE,"E60.MirrorCS")])]})])],"derivedFrom":makeQuery(id+"F30.opExtrude","CAP_EDGE",EDGE,{"disambiguationData":[OSD([subQ0])],"isStart":true})});}
            chamfer(context, id + "F34", {"entities" : qUnion([Q0, Q1]), "chamferType" : ChamferType.OFFSET_ANGLE, "width" : 10 * mm, "oppositeDirection" : false, "angle" : 30 * degree, "tangentPropagation" : true});
        }
    });
